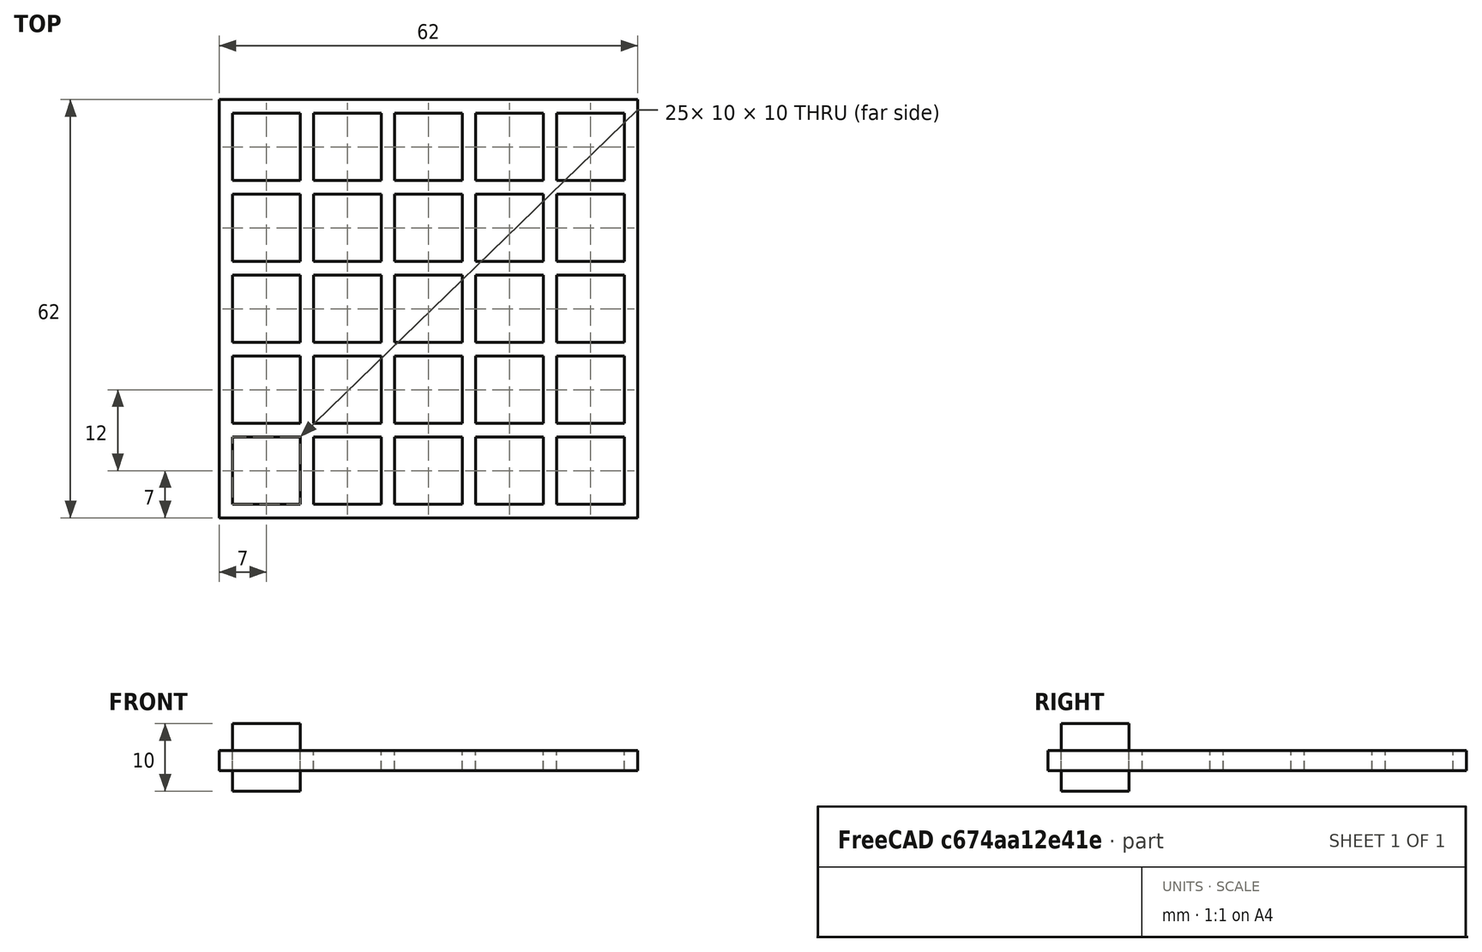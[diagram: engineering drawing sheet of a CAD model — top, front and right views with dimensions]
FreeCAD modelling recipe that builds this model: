
FCSTD DOCUMENT  (FreeCAD 0.21R33694 (Git))
Label: OJT1_T010P09_Y
License: All rights reserved
LicenseURL: http://en.wikipedia.org/wiki/All_rights_reserved
objects: Part::Box×2, Part::FeaturePython×1, Part::Cut×1
note: 3 computed .brp shape members not serialized (recipe doc carries the construction recipe); baked Part::Feature solids carry a one-line shape summary decoded from their .brp

FEATURE [Part::Box] Box  label="Cube"
  AttacherType = Attacher::AttachEngine3D
  Height = 10
  Length = 10
  Width = 10
FEATURE [Part::FeaturePython] Array  # Draft array (typed FeaturePython)
  AlwaysSyncPlacement = false
  Angle = 360
  ArrayType = 0
  Axis = (0,0,1)
  Base = -> Box
  Center = (0,0,0)
  Count = 25
  ExpandArray = false
  Fuse = false
  IntervalAxis = (0,0,0)
  IntervalX = (12,0,0)
  IntervalY = (0,12,0)
  IntervalZ = (0,0,100)
  NumberCircles = 3
  NumberPolar = 5
  NumberX = 5
  NumberY = 5
  NumberZ = 1
  PlacementList = 25 placements: [(0,0,0),(0,12,0),(0,24,0),(0,36,0),(0,48,0),(12,0,0),(12,12,0),(12,24,0),(12,36,0),(12,48,0),(24,0,0),(24,12,0),(24,24,0),(24,36,0),(24,48,0),(36,0,0),(36,12,0),(36,24,0),(36,36,0),(36,48,0),(48,0,0),(48,12,0),(48,24,0),(48,36,0),(48,48,0)]
  RadialDistance = 50
  ScaleList = (25) [(1,1,1),(1,1,1),(1,1,1),(1,1,1),(1,1,1),(1,1,1),(1,1,1),(1,1,1),(1,1,1),(1,1,1),(1,1,1),(1,1,1),(1,1,1),(1,1,1),(1,1,1),(1,1,1),(1,1,1),(1,1,1),+7 more]
  Symmetry = 1
  TangentialDistance = 25
FEATURE [Part::Box] Box001  label="Cube001"
  AttacherType = Attacher::AttachEngine3D
  Height = 3
  Length = 62
  Placement = pos=(-2,-2,3) rot=(0,0,1;0rad)
  Width = 62
FEATURE [Part::Cut] Cut
  Base = -> Box001
  Refine = true
  Tool = -> Array
